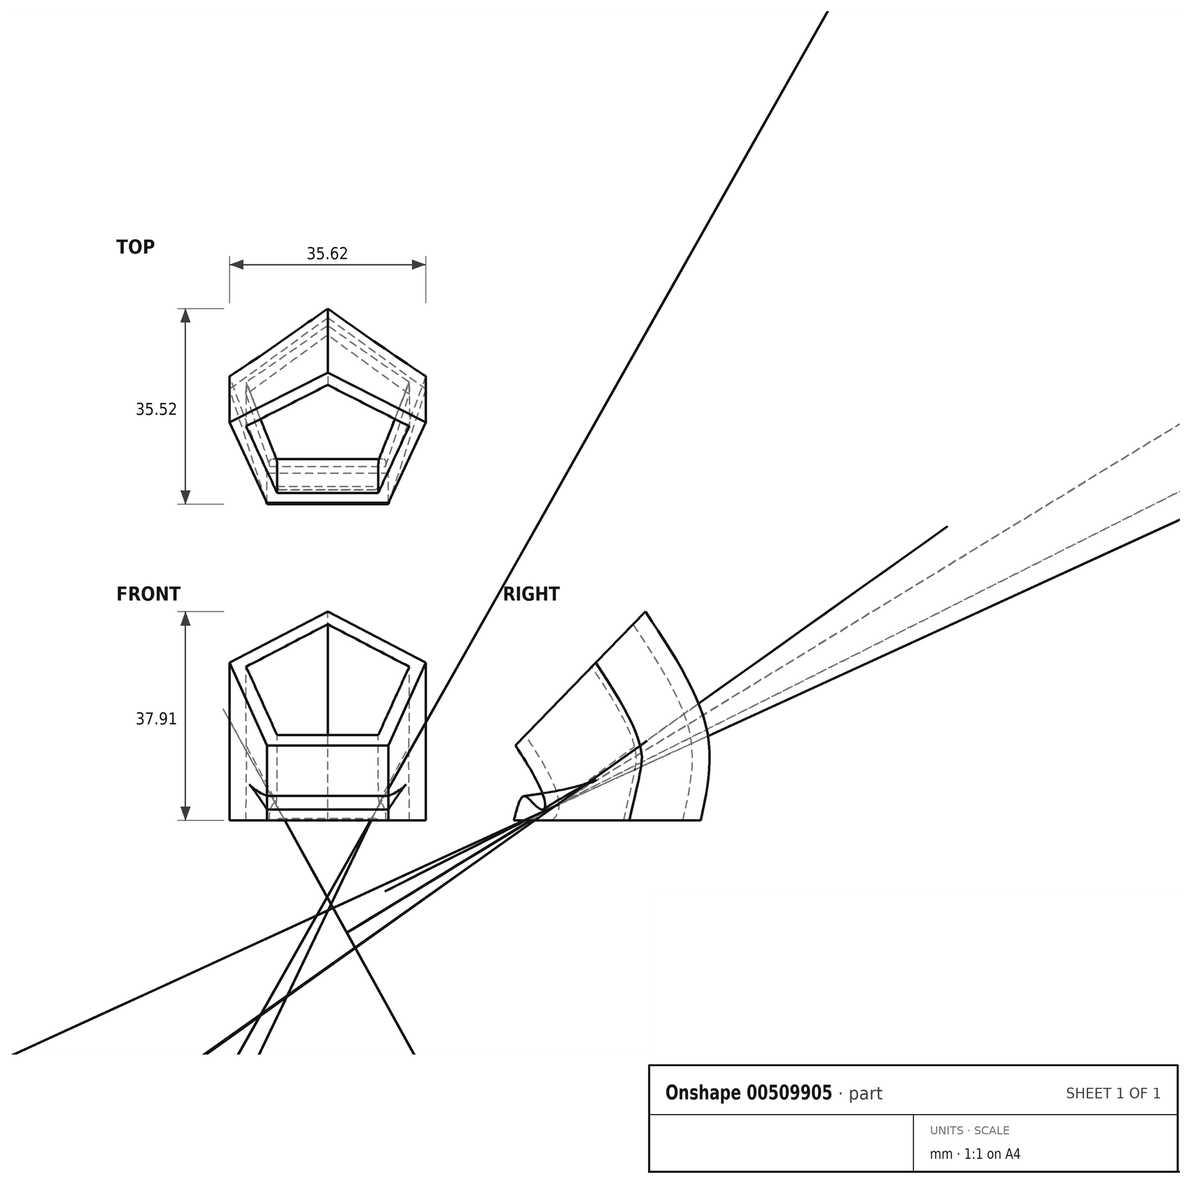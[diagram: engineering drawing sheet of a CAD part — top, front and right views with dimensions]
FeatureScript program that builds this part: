
annotation { "Feature Type Name" : "Feature", "Feature Type Description" : "" }
export const myFeature = defineFeature(function(context is Context, id is Id, definition is map)
    precondition{}
    {
        {
            var Q0;
            Q0=qCreatedBy(makeId("Right.planeOp"),FACE);
            var sketch = newSketch(context, id + "F0", { "sketchPlane" : qUnion([Q0])});
            skFitSpline(sketch, "E0", {"points": [v(39.54, 0) * mm, v(40.7, 16.28) * mm, v(29.54, 37.91) * mm], "startDerivative": vector(7.74, 35.45) * mm, "endDerivative": vector(-26.6, 40.22) * mm});
            skSolve(sketch);
        }
        {
            var Q0;
            Q0=qCreatedBy(makeId("Top.planeOp"),FACE);
            var sketch = newSketch(context, id + "F1", { "sketchPlane" : qUnion([Q0])});
            skCircle(sketch, "E1.cCircle", {"center": v(0, 20.81) * mm, "radius": 15.15 * mm, "construction": true});
            skLineSegment(sketch, "E1.0", {"start": v(17.8, 26.6) * mm, "end": v(11, 5.66) * mm});
            skLineSegment(sketch, "E1.1", {"start": v(11, 5.66) * mm, "end": v(-11, 5.66) * mm});
            skLineSegment(sketch, "E1.2", {"start": v(-11, 5.66) * mm, "end": v(-17.8, 26.6) * mm});
            skLineSegment(sketch, "E1.3", {"start": v(-17.8, 26.6) * mm, "end": v(0, 39.54) * mm});
            skLineSegment(sketch, "E1.4", {"start": v(0, 39.54) * mm, "end": v(17.8, 26.6) * mm});
            skPoint(sketch, "E1.0.midPoint", {"position": v(14.4, 16.13) * mm});
            skPoint(sketch, "E2", {"position": v(0, 5.66) * mm});
            skSolve(sketch);
        }
        {
            var Q0;
            Q0=makeQuery(id+"F1.imprint","IMPRINT",FACE,{"disambiguationData":[TD([[makeQuery(id+"F1.imprint","IMPRINT",EDGE,{"derivedFrom":sQuery(id+"F1.wireOp",EDGE,"E1.0")}),-1.0]])]});
            var Q1;
            Q1=sQuery(id+"F0.wireOp",EDGE,"E0");
            sweep(context, id + "F2", {"profiles" : qUnion([Q0]), "path" : qUnion([Q1])});
        }
        {
            var Q0;
            Q0=makeQuery(id+"F2.opSweep","CAP_FACE",FACE,{"disambiguationData":[OSD([sQuery(id+"F1.wireOp",EDGE,"E1.0"),sQuery(id+"F1.wireOp",EDGE,"E1.1"),sQuery(id+"F1.wireOp",EDGE,"E1.2"),sQuery(id+"F1.wireOp",EDGE,"E1.3"),sQuery(id+"F1.wireOp",EDGE,"E1.4"),sQuery(id+"F0.wireOp",VERTEX,"6J3YBVpC-q25J-ciJ0-YPuk-U9wen0dbhdMu.end")])],"isStart":false});
            var Q1;
            Q1=makeQuery(id+"F2.opSweep","CAP_FACE",FACE,{"disambiguationData":[OSD([sQuery(id+"F1.wireOp",EDGE,"E1.0"),sQuery(id+"F1.wireOp",EDGE,"E1.1"),sQuery(id+"F1.wireOp",EDGE,"E1.2"),sQuery(id+"F1.wireOp",EDGE,"E1.3"),sQuery(id+"F1.wireOp",EDGE,"E1.4"),sQuery(id+"F0.wireOp",VERTEX,"6J3YBVpC-q25J-ciJ0-YPuk-U9wen0dbhdMu.start")])],"isStart":true});
            shell(context, id + "F3", {"entities" : qUnion([Q0, Q1]), "thickness" : 2.54 * mm});
        }
    });
